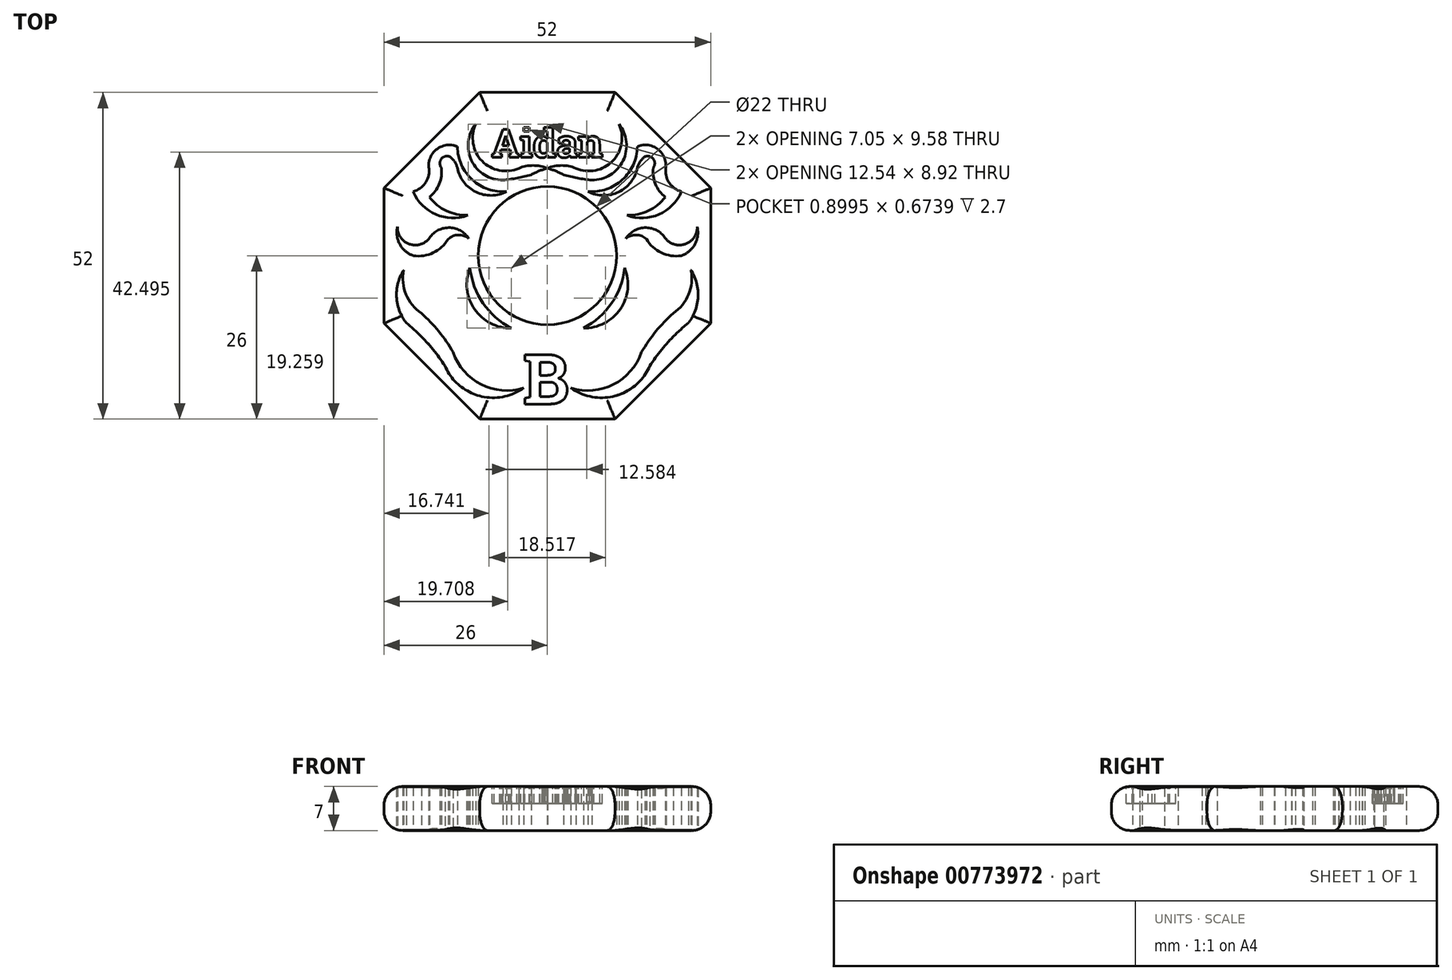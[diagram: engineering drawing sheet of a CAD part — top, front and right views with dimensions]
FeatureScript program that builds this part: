
annotation { "Feature Type Name" : "Feature", "Feature Type Description" : "" }
export const myFeature = defineFeature(function(context is Context, id is Id, definition is map)
    precondition{}
    {
        {
            var Q0;
            Q0=qCreatedBy(makeId("Top.planeOp"),FACE);
            var sketch = newSketch(context, id + "F0", { "sketchPlane" : qUnion([Q0])});
            skCircle(sketch, "E0", {"center": v(0, 0) * mm, "radius": 11 * mm});
            skLineSegment(sketch, "E1.0", {"start": v(-26, -10.77) * mm, "end": v(-26, 10.77) * mm});
            skLineSegment(sketch, "E1.1", {"start": v(-26, 10.77) * mm, "end": v(-10.77, 26) * mm});
            skLineSegment(sketch, "E1.2", {"start": v(-10.77, 26) * mm, "end": v(10.77, 26) * mm});
            skLineSegment(sketch, "E1.3", {"start": v(10.77, 26) * mm, "end": v(26, 10.77) * mm});
            skLineSegment(sketch, "E1.4", {"start": v(26, 10.77) * mm, "end": v(26, -10.77) * mm});
            skLineSegment(sketch, "E1.5", {"start": v(26, -10.77) * mm, "end": v(10.77, -26) * mm});
            skLineSegment(sketch, "E1.6", {"start": v(10.77, -26) * mm, "end": v(-10.77, -26) * mm});
            skLineSegment(sketch, "E1.7", {"start": v(-10.77, -26) * mm, "end": v(-26, -10.77) * mm});
            skPoint(sketch, "E1.0.midPoint", {"position": v(-26, 0) * mm});
            skArc(sketch, "E2", {"start": v(-12.5, 2.74) * mm, "mid": v(-15.71, 4.46) * mm, "end": v(-18.88, 2.65) * mm});
            skArc(sketch, "E3", {"start": v(-23.86, 4.62) * mm, "mid": v(-22.06, 1.9) * mm, "end": v(-18.88, 2.65) * mm});
            skArc(sketch, "E4", {"start": v(-23.86, 4.62) * mm, "mid": v(-23.48, 1.82) * mm, "end": v(-21.32, 0) * mm});
            skArc(sketch, "E5", {"start": v(-21.32, 0) * mm, "mid": v(-18.15, 0.48) * mm, "end": v(-15.78, 2.65) * mm});
            skArc(sketch, "E6", {"start": v(-12.5, 2.74) * mm, "mid": v(-14.16, 3.3) * mm, "end": v(-15.78, 2.65) * mm});
            skLineSegment(sketch, "E7", {"start": v(0, 26) * mm, "end": v(0, -26) * mm, "construction": true});
            skLineSegment(sketch, "E8", {"start": v(-26, 0) * mm, "end": v(26, 0) * mm, "construction": true});
            skArc(sketch, "E9.MirrorCS", {"start": v(23.86, 4.62) * mm, "mid": v(23.48, 1.82) * mm, "end": v(21.32, 0) * mm});
            skArc(sketch, "E10.MirrorCS", {"start": v(23.86, 4.62) * mm, "mid": v(22.06, 1.9) * mm, "end": v(18.88, 2.65) * mm});
            skArc(sketch, "E11.MirrorCS", {"start": v(12.5, 2.74) * mm, "mid": v(14.16, 3.3) * mm, "end": v(15.78, 2.65) * mm});
            skArc(sketch, "E12.MirrorCS", {"start": v(21.32, 0) * mm, "mid": v(18.15, 0.48) * mm, "end": v(15.78, 2.65) * mm});
            skArc(sketch, "E13.MirrorCS", {"start": v(12.5, 2.74) * mm, "mid": v(15.71, 4.46) * mm, "end": v(18.88, 2.65) * mm});
            skArc(sketch, "E14", {"start": v(-12.3, -1.95) * mm, "mid": v(-10.23, -7.57) * mm, "end": v(-5.74, -11.53) * mm});
            skArc(sketch, "E15", {"start": v(-12.3, -1.95) * mm, "mid": v(-11.6, -8.51) * mm, "end": v(-5.74, -11.53) * mm});
            skArc(sketch, "E16.MirrorCS", {"start": v(12.3, -1.95) * mm, "mid": v(11.6, -8.51) * mm, "end": v(5.74, -11.53) * mm});
            skArc(sketch, "E17.MirrorCS", {"start": v(12.3, -1.95) * mm, "mid": v(10.23, -7.57) * mm, "end": v(5.74, -11.53) * mm});
            skArc(sketch, "E18", {"start": v(-11.39, 20.95) * mm, "mid": v(-10.4, 15.07) * mm, "end": v(-4.54, 13.91) * mm});
            skArc(sketch, "E19", {"start": v(-11.39, 20.95) * mm, "mid": v(-12.05, 15.13) * mm, "end": v(-7.07, 12.04) * mm});
            skArc(sketch, "E20", {"start": v(-7.07, 12.04) * mm, "mid": v(-4.8, 12.36) * mm, "end": v(-2.56, 12.88) * mm});
            skArc(sketch, "E21", {"start": v(-0.02, 13.91) * mm, "mid": v(-1.32, 13.48) * mm, "end": v(-2.56, 12.88) * mm});
            skArc(sketch, "E22", {"start": v(-0.02, 13.91) * mm, "mid": v(-2.28, 14.37) * mm, "end": v(-4.54, 13.91) * mm});
            skArc(sketch, "E23.MirrorCS", {"start": v(11.39, 20.95) * mm, "mid": v(12.05, 15.13) * mm, "end": v(7.07, 12.04) * mm});
            skArc(sketch, "E24.MirrorCS", {"start": v(11.39, 20.95) * mm, "mid": v(10.4, 15.07) * mm, "end": v(4.54, 13.91) * mm});
            skArc(sketch, "E25.MirrorCS", {"start": v(7.07, 12.04) * mm, "mid": v(4.8, 12.36) * mm, "end": v(2.56, 12.88) * mm});
            skArc(sketch, "E26.MirrorCS", {"start": v(0.02, 13.91) * mm, "mid": v(1.32, 13.48) * mm, "end": v(2.56, 12.88) * mm});
            skArc(sketch, "E27.MirrorCS", {"start": v(0.02, 13.91) * mm, "mid": v(2.28, 14.37) * mm, "end": v(4.54, 13.91) * mm});
            skArc(sketch, "E28", {"start": v(-22.86, -2.3) * mm, "mid": v(-24, -6.56) * mm, "end": v(-22.45, -10.7) * mm});
            skArc(sketch, "E29", {"start": v(-16.3, -17.55) * mm, "mid": v(-19.1, -13.88) * mm, "end": v(-22.45, -10.7) * mm});
            skArc(sketch, "E30", {"start": v(-16.3, -17.55) * mm, "mid": v(-10.86, -22.3) * mm, "end": v(-3.75, -21.06) * mm});
            skArc(sketch, "E31", {"start": v(-22.86, -2.3) * mm, "mid": v(-22.49, -6.15) * mm, "end": v(-20.05, -9.16) * mm});
            skArc(sketch, "E32", {"start": v(-15, -15.35) * mm, "mid": v(-17.28, -12.06) * mm, "end": v(-20.05, -9.16) * mm});
            skArc(sketch, "E33", {"start": v(-15, -15.35) * mm, "mid": v(-10.53, -20.48) * mm, "end": v(-3.75, -21.06) * mm});
            skArc(sketch, "E34.MirrorCS", {"start": v(15, -15.35) * mm, "mid": v(10.53, -20.48) * mm, "end": v(3.75, -21.06) * mm});
            skArc(sketch, "E35.MirrorCS", {"start": v(22.86, -2.3) * mm, "mid": v(24, -6.56) * mm, "end": v(22.45, -10.7) * mm});
            skArc(sketch, "E36.MirrorCS", {"start": v(16.3, -17.55) * mm, "mid": v(19.1, -13.88) * mm, "end": v(22.45, -10.7) * mm});
            skArc(sketch, "E37.MirrorCS", {"start": v(15, -15.35) * mm, "mid": v(17.28, -12.06) * mm, "end": v(20.05, -9.16) * mm});
            skArc(sketch, "E38.MirrorCS", {"start": v(16.3, -17.55) * mm, "mid": v(10.86, -22.3) * mm, "end": v(3.75, -21.06) * mm});
            skArc(sketch, "E39.MirrorCS", {"start": v(22.86, -2.3) * mm, "mid": v(22.49, -6.15) * mm, "end": v(20.05, -9.16) * mm});
            skArc(sketch, "E40", {"start": v(-14.32, 17.36) * mm, "mid": v(-11.94, 12.1) * mm, "end": v(-6.48, 10.21) * mm});
            skArc(sketch, "E41", {"start": v(-14.32, 17.36) * mm, "mid": v(-17.56, 16.99) * mm, "end": v(-18.86, 14) * mm});
            skArc(sketch, "E42", {"start": v(-21.33, 10.21) * mm, "mid": v(-19.37, 11.63) * mm, "end": v(-18.86, 14) * mm});
            skArc(sketch, "E43", {"start": v(-21.33, 10.21) * mm, "mid": v(-17.76, 6.58) * mm, "end": v(-12.67, 6.43) * mm});
            skArc(sketch, "E44", {"start": v(-18.78, 9.32) * mm, "mid": v(-16.06, 7.15) * mm, "end": v(-12.67, 6.43) * mm});
            skArc(sketch, "E45", {"start": v(-18.78, 9.32) * mm, "mid": v(-17.2, 11.4) * mm, "end": v(-16.86, 14) * mm});
            skArc(sketch, "E46", {"start": v(-15.55, 15.78) * mm, "mid": v(-16.88, 15.38) * mm, "end": v(-16.86, 14) * mm});
            skArc(sketch, "E47", {"start": v(-14.32, 14) * mm, "mid": v(-14.78, 15) * mm, "end": v(-15.55, 15.78) * mm});
            skArc(sketch, "E48", {"start": v(-14.32, 14) * mm, "mid": v(-11.35, 10.13) * mm, "end": v(-6.48, 10.21) * mm});
            skArc(sketch, "E49.MirrorCS", {"start": v(21.33, 10.21) * mm, "mid": v(17.76, 6.58) * mm, "end": v(12.67, 6.43) * mm});
            skArc(sketch, "E50.MirrorCS", {"start": v(14.32, 17.36) * mm, "mid": v(17.56, 16.99) * mm, "end": v(18.86, 14) * mm});
            skArc(sketch, "E51.MirrorCS", {"start": v(15.55, 15.78) * mm, "mid": v(16.88, 15.38) * mm, "end": v(16.86, 14) * mm});
            skArc(sketch, "E52.MirrorCS", {"start": v(14.32, 14) * mm, "mid": v(11.35, 10.13) * mm, "end": v(6.48, 10.21) * mm});
            skArc(sketch, "E53.MirrorCS", {"start": v(21.33, 10.21) * mm, "mid": v(19.37, 11.63) * mm, "end": v(18.86, 14) * mm});
            skArc(sketch, "E54.MirrorCS", {"start": v(18.78, 9.32) * mm, "mid": v(16.06, 7.15) * mm, "end": v(12.67, 6.43) * mm});
            skArc(sketch, "E55.MirrorCS", {"start": v(14.32, 14) * mm, "mid": v(14.78, 15) * mm, "end": v(15.55, 15.78) * mm});
            skArc(sketch, "E56.MirrorCS", {"start": v(14.32, 17.36) * mm, "mid": v(11.94, 12.1) * mm, "end": v(6.48, 10.21) * mm});
            skArc(sketch, "E57.MirrorCS", {"start": v(18.78, 9.32) * mm, "mid": v(17.2, 11.4) * mm, "end": v(16.86, 14) * mm});
            skSolve(sketch);
        }
        {
            var Q0;
            Q0=qSketchRegion(id+"F0",true);
            extrude(context, id + "F1", {"entities" : qUnion([Q0]), "depth" : 7 * mm, "offsetDistance" : 25 * mm});
        }
        {
            var Q0;
            Q0=makeQuery(id+"F1.opExtrude","CAP_FACE",FACE,{"disambiguationData":[OSD([sQuery(id+"F0.wireOp",EDGE,"E0"),sQuery(id+"F0.wireOp",EDGE,"E1.0"),sQuery(id+"F0.wireOp",EDGE,"E1.1"),sQuery(id+"F0.wireOp",EDGE,"E1.2"),sQuery(id+"F0.wireOp",EDGE,"E1.3"),sQuery(id+"F0.wireOp",EDGE,"E1.4"),sQuery(id+"F0.wireOp",EDGE,"E1.5"),sQuery(id+"F0.wireOp",EDGE,"E1.6"),sQuery(id+"F0.wireOp",EDGE,"E1.7"),sQuery(id+"F0.wireOp",EDGE,"E2"),sQuery(id+"F0.wireOp",EDGE,"E3"),sQuery(id+"F0.wireOp",EDGE,"E4"),sQuery(id+"F0.wireOp",EDGE,"E5"),sQuery(id+"F0.wireOp",EDGE,"E6"),sQuery(id+"F0.wireOp",EDGE,"E9.MirrorCS"),sQuery(id+"F0.wireOp",EDGE,"E10.MirrorCS"),sQuery(id+"F0.wireOp",EDGE,"E11.MirrorCS"),sQuery(id+"F0.wireOp",EDGE,"E12.MirrorCS"),sQuery(id+"F0.wireOp",EDGE,"E13.MirrorCS"),sQuery(id+"F0.wireOp",EDGE,"E14"),sQuery(id+"F0.wireOp",EDGE,"E15"),sQuery(id+"F0.wireOp",EDGE,"E16.MirrorCS"),sQuery(id+"F0.wireOp",EDGE,"E17.MirrorCS"),sQuery(id+"F0.wireOp",EDGE,"E18"),sQuery(id+"F0.wireOp",EDGE,"E19"),sQuery(id+"F0.wireOp",EDGE,"E20"),sQuery(id+"F0.wireOp",EDGE,"E21"),sQuery(id+"F0.wireOp",EDGE,"E22"),sQuery(id+"F0.wireOp",EDGE,"E23.MirrorCS"),sQuery(id+"F0.wireOp",EDGE,"E24.MirrorCS"),sQuery(id+"F0.wireOp",EDGE,"E25.MirrorCS"),sQuery(id+"F0.wireOp",EDGE,"E26.MirrorCS"),sQuery(id+"F0.wireOp",EDGE,"E27.MirrorCS")])],"isStart":false});
            var sketch = newSketch(context, id + "F2", { "sketchPlane" : qUnion([Q0])});
            skText(sketch, "E58", { "text": "Aidan", "fontName": "RobotoSlab-Bold.ttf"});
            skText(sketch, "E59", { "text": "B", "fontName": "RobotoSlab-Bold.ttf"});
            skLineSegment(sketch, "E60", {"start": v(0, 26) * mm, "end": v(0, -26) * mm, "construction": true});
            skLineSegment(sketch, "E61", {"start": v(-26, 0) * mm, "end": v(26, 0) * mm, "construction": true});
            const initialGuessF2  = {"E58": [-0.0089, 0.01564, 1, 0, 0.00454], "E59": [-0.00389, -0.02362, 1, 0, 0.00798]};
            skSetInitialGuess(sketch, initialGuessF2);
            skSolve(sketch);
        }
        {
            var Q0;
            Q0=qSketchRegion(id+"F2",true);
            extrude(context, id + "F3", {"entities" : qUnion([Q0]), "operationType" : NewBodyOperationType.REMOVE, "oppositeDirection" : true, "depth" : 2.7 * mm, "offsetDistance" : 25 * mm});
        }
        {
            var Q0;
            Q0=makeQuery(id+"F1.opExtrude","CAP_EDGE",EDGE,{"disambiguationData":[OSD([sQuery(id+"F0.wireOp",EDGE,"E1.2")])],"isStart":false});
            var Q1;
            Q1=makeQuery(id+"F1.opExtrude","CAP_EDGE",EDGE,{"disambiguationData":[OSD([sQuery(id+"F0.wireOp",EDGE,"E1.1")])],"isStart":false});
            var Q2;
            Q2=makeQuery(id+"F1.opExtrude","CAP_EDGE",EDGE,{"disambiguationData":[OSD([sQuery(id+"F0.wireOp",EDGE,"E1.7")])],"isStart":false});
            var Q3;
            Q3=makeQuery(id+"F1.opExtrude","CAP_EDGE",EDGE,{"disambiguationData":[OSD([sQuery(id+"F0.wireOp",EDGE,"E1.6")])],"isStart":false});
            var Q4;
            Q4=makeQuery(id+"F1.opExtrude","CAP_EDGE",EDGE,{"disambiguationData":[OSD([sQuery(id+"F0.wireOp",EDGE,"E1.5")])],"isStart":false});
            var Q5;
            Q5=makeQuery(id+"F1.opExtrude","CAP_EDGE",EDGE,{"disambiguationData":[OSD([sQuery(id+"F0.wireOp",EDGE,"E1.4")])],"isStart":false});
            var Q6;
            Q6=makeQuery(id+"F1.opExtrude","CAP_EDGE",EDGE,{"disambiguationData":[OSD([sQuery(id+"F0.wireOp",EDGE,"E1.3")])],"isStart":false});
            var Q7;
            Q7=makeQuery(id+"F1.opExtrude","CAP_EDGE",EDGE,{"disambiguationData":[OSD([sQuery(id+"F0.wireOp",EDGE,"E1.1")])],"isStart":true});
            var Q8;
            Q8=makeQuery(id+"F1.opExtrude","CAP_EDGE",EDGE,{"disambiguationData":[OSD([sQuery(id+"F0.wireOp",EDGE,"E1.0")])],"isStart":true});
            var Q9;
            Q9=makeQuery(id+"F1.opExtrude","CAP_EDGE",EDGE,{"disambiguationData":[OSD([sQuery(id+"F0.wireOp",EDGE,"E1.7")])],"isStart":true});
            var Q10;
            Q10=makeQuery(id+"F1.opExtrude","CAP_EDGE",EDGE,{"disambiguationData":[OSD([sQuery(id+"F0.wireOp",EDGE,"E1.6")])],"isStart":true});
            var Q11;
            Q11=makeQuery(id+"F1.opExtrude","CAP_EDGE",EDGE,{"disambiguationData":[OSD([sQuery(id+"F0.wireOp",EDGE,"E1.5")])],"isStart":true});
            var Q12;
            Q12=makeQuery(id+"F1.opExtrude","CAP_EDGE",EDGE,{"disambiguationData":[OSD([sQuery(id+"F0.wireOp",EDGE,"E1.4")])],"isStart":true});
            var Q13;
            Q13=makeQuery(id+"F1.opExtrude","CAP_EDGE",EDGE,{"disambiguationData":[OSD([sQuery(id+"F0.wireOp",EDGE,"E1.3")])],"isStart":true});
            var Q14;
            Q14=makeQuery(id+"F1.opExtrude","CAP_EDGE",EDGE,{"disambiguationData":[OSD([sQuery(id+"F0.wireOp",EDGE,"E1.2")])],"isStart":true});
            var Q15;
            Q15=makeQuery(id+"F1.opExtrude","CAP_EDGE",EDGE,{"disambiguationData":[OSD([sQuery(id+"F0.wireOp",EDGE,"E1.0")])],"isStart":false});
            fillet(context, id + "F4", {"entities" : qUnion([Q0, Q1, Q2, Q3, Q4, Q5, Q6, Q7, Q8, Q9, Q10, Q11, Q12, Q13, Q14, Q15]), "radius" : 3 * mm, "tangentPropagation" : true, "allowEdgeOverflow" : false});
        }
    });
